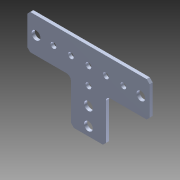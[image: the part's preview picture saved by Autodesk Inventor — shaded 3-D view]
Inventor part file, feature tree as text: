
AUTODESK INVENTOR PART (.ipt)
format: ipt  version: 2015 SP1 (Build 190203100, 203)  size: 175,616 bytes
history: native  units: in
note: dims shown in document units (in); Inventor stores cm internally (conversion verified against a paired STEP export)
features: extrude x2, sketch x2, projected_geometry x2, fillet x1, other x1, imported_body x1
ambient origin geometry x8: Origin, YZ Plane, XZ Plane, XY Plane, X Axis, Y Axis, Z Axis, Center Point
bodies: Body1 (feature_tree)
feature tree (9):
  fillet  "Fillet1"  Radius=0.25in
  other  "VersaFrame Gusset (217-3557)1"
  extrude  "Extrusion1"  Depth=1.0in TaperAngle=0.0deg
  extrude  "Extrusion2"  Depth=1.0in
  imported_body  "Base1"
  sketch  "Sketch1"  dims[d1=0.25in d2=1.0in d3=0.0in]
  projected_geometry  "Projected Loop1"
  sketch  "Sketch2"  dims[d4=0.25in d5=0.25in d6=1.0in d7=0.0in]
  projected_geometry  "Projected Loop2"
